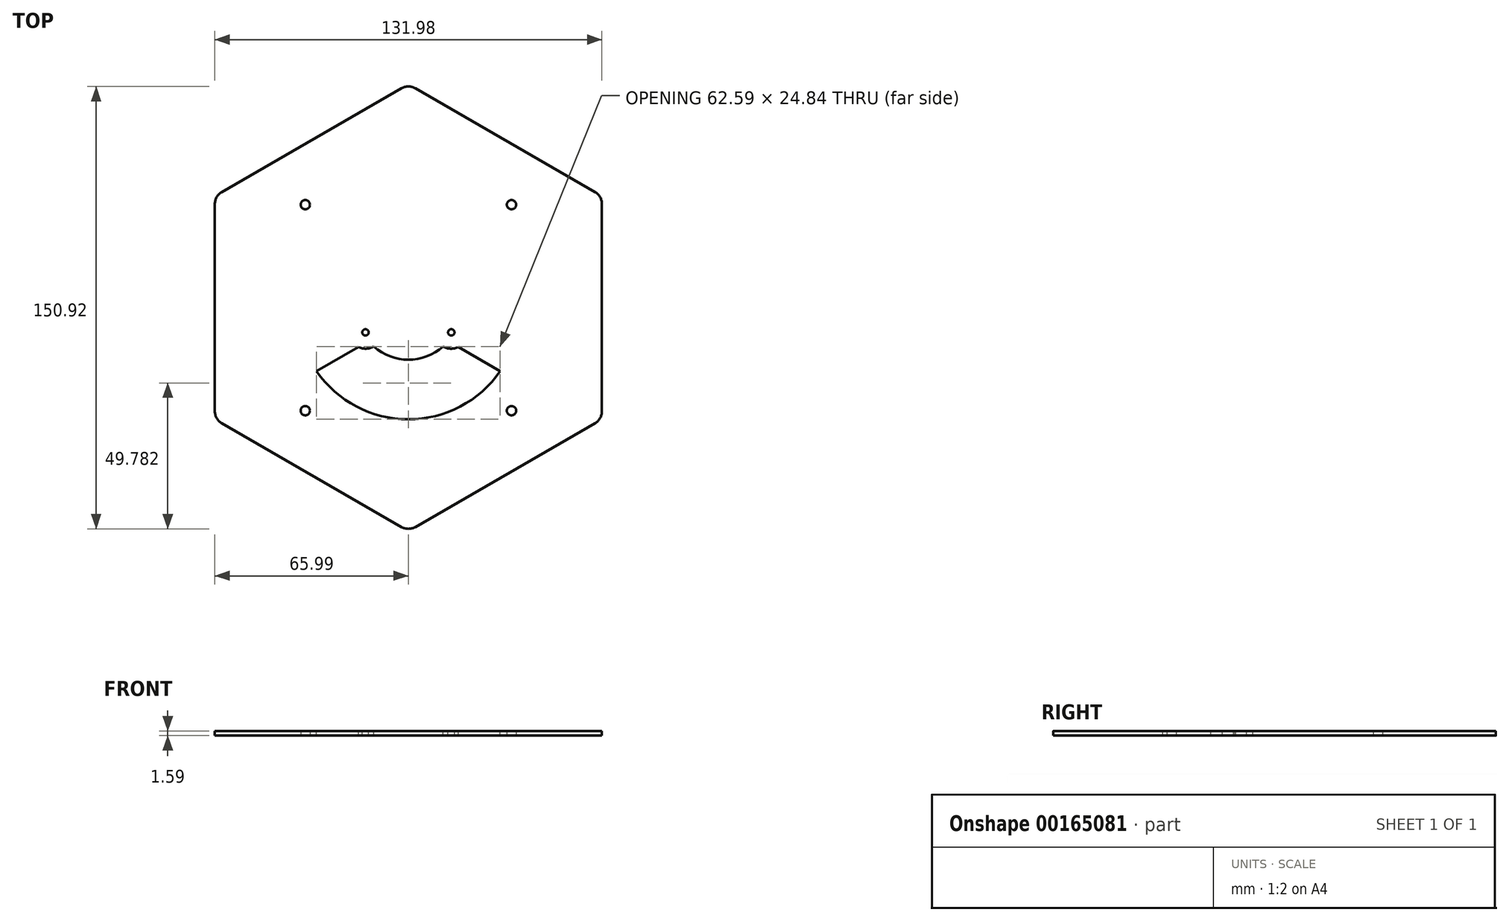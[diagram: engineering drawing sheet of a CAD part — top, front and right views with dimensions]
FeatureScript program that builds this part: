
annotation { "Feature Type Name" : "Feature", "Feature Type Description" : "" }
export const myFeature = defineFeature(function(context is Context, id is Id, definition is map)
    precondition{}
    {
        {
            var Q0;
            Q0=qCreatedBy(makeId("Top.planeOp"),FACE);
            var sketch = newSketch(context, id + "F0", { "sketchPlane" : qUnion([Q0])});
            skLineSegment(sketch, "E0.bottom", {"start": v(35.15, -35.15) * mm, "end": v(35.15, 35.15) * mm, "construction": true});
            skLineSegment(sketch, "E0.top", {"start": v(-35.15, -35.15) * mm, "end": v(-35.15, 35.15) * mm, "construction": true});
            skLineSegment(sketch, "E0.left", {"start": v(35.15, -35.15) * mm, "end": v(-35.15, -35.15) * mm, "construction": true});
            skLineSegment(sketch, "E0.right", {"start": v(35.15, 35.15) * mm, "end": v(-35.15, 35.15) * mm, "construction": true});
            skPoint(sketch, "E0.middle", {"position": v(0, 0) * mm});
            skCircle(sketch, "E1", {"center": v(0, 0) * mm, "radius": 38.1 * mm, "construction": true});
            skCircle(sketch, "E2", {"center": v(35.15, -35.15) * mm, "radius": 1.59 * mm});
            skCircle(sketch, "E3", {"center": v(35.15, 35.15) * mm, "radius": 1.59 * mm});
            skCircle(sketch, "E4", {"center": v(-35.15, 35.15) * mm, "radius": 1.59 * mm});
            skCircle(sketch, "E5", {"center": v(-35.15, -35.15) * mm, "radius": 1.59 * mm});
            skCircle(sketch, "E6", {"center": v(35.15, -35.15) * mm, "radius": 4.53 * mm, "construction": true});
            skCircle(sketch, "E7.cCircle", {"center": v(0, 0) * mm, "radius": 66 * mm, "construction": true});
            skLineSegment(sketch, "E7.0", {"start": v(66, 38.1) * mm, "end": v(66, -38.1) * mm});
            skLineSegment(sketch, "E7.1", {"start": v(66, -38.1) * mm, "end": v(0, -76.2) * mm});
            skLineSegment(sketch, "E7.2", {"start": v(0, -76.2) * mm, "end": v(-66, -38.1) * mm});
            skLineSegment(sketch, "E7.3", {"start": v(-66, -38.1) * mm, "end": v(-66, 38.1) * mm});
            skLineSegment(sketch, "E7.4", {"start": v(-66, 38.1) * mm, "end": v(0, 76.2) * mm});
            skLineSegment(sketch, "E7.5", {"start": v(0, 76.2) * mm, "end": v(66, 38.1) * mm});
            skPoint(sketch, "E7.0.midPoint", {"position": v(66, 0) * mm});
            skCircle(sketch, "E8.cCircle", {"center": v(0, 0) * mm, "radius": 52.55 * mm, "construction": true});
            skLineSegment(sketch, "E8.0", {"start": v(52.55, 30.34) * mm, "end": v(52.55, -30.34) * mm, "construction": true});
            skLineSegment(sketch, "E8.1", {"start": v(52.55, -30.34) * mm, "end": v(0, -60.68) * mm, "construction": true});
            skLineSegment(sketch, "E8.2", {"start": v(0, -60.68) * mm, "end": v(-52.55, -30.34) * mm, "construction": true});
            skLineSegment(sketch, "E8.3", {"start": v(-52.55, -30.34) * mm, "end": v(-52.55, 30.34) * mm, "construction": true});
            skLineSegment(sketch, "E8.4", {"start": v(-52.55, 30.34) * mm, "end": v(0, 60.68) * mm, "construction": true});
            skLineSegment(sketch, "E8.5", {"start": v(0, 60.68) * mm, "end": v(52.55, 30.34) * mm, "construction": true});
            skPoint(sketch, "E8.0.midPoint", {"position": v(52.55, 0) * mm});
            skSolve(sketch);
        }
        {
            var Q0;
            Q0=makeQuery(id+"F0.imprint","IMPRINT",FACE,{"disambiguationData":[TD([[makeQuery(id+"F0.imprint","IMPRINT",EDGE,{"derivedFrom":sQuery(id+"F0.wireOp",EDGE,"E1")}),-1.0]])]});
            var Q1;
            Q1=makeQuery(id+"F0.imprint","IMPRINT",FACE,{"disambiguationData":[TD([[makeQuery(id+"F0.imprint","IMPRINT",EDGE,{"derivedFrom":sQuery(id+"F0.wireOp",EDGE,"E2")}),-1.0]])]});
            extrude(context, id + "F1", {"entities" : qUnion([Q0, Q1]), "depth" : 1.59 * mm});
        }
        {
            var Q0;
            Q0=makeQuery(id+"F1.opExtrude","CAP_FACE",FACE,{"disambiguationData":[OSD([sQuery(id+"F0.wireOp",EDGE,"E2"),sQuery(id+"F0.wireOp",EDGE,"E3"),sQuery(id+"F0.wireOp",EDGE,"E4"),sQuery(id+"F0.wireOp",EDGE,"E5"),sQuery(id+"F0.wireOp",EDGE,"R1JFTZ4v-WKVF-8XfW-xGAy-tLIKOYTsBxTY.bottom"),sQuery(id+"F0.wireOp",EDGE,"R1JFTZ4v-WKVF-8XfW-xGAy-tLIKOYTsBxTY.top"),sQuery(id+"F0.wireOp",EDGE,"R1JFTZ4v-WKVF-8XfW-xGAy-tLIKOYTsBxTY.left"),sQuery(id+"F0.wireOp",EDGE,"R1JFTZ4v-WKVF-8XfW-xGAy-tLIKOYTsBxTY.right")])],"isStart":false});
            var sketch = newSketch(context, id + "F2", { "sketchPlane" : qUnion([Q0])});
            skArc(sketch, "E9", {"start": v(-11.85, -13.26) * mm, "mid": v(0, -17.78) * mm, "end": v(11.85, -13.26) * mm});
            skArc(sketch, "E10", {"start": v(-31.3, -21.73) * mm, "mid": v(0, -38.1) * mm, "end": v(31.3, -21.73) * mm});
            skLineSegment(sketch, "E11", {"start": v(0, -17.78) * mm, "end": v(0, 0) * mm, "construction": true});
            skArc(sketch, "E12", {"start": v(11.85, -13.26) * mm, "mid": v(14.4, -14) * mm, "end": v(16.99, -13.47) * mm});
            skLineSegment(sketch, "E13", {"start": v(11.85, -13.26) * mm, "end": v(14.63, -8.44) * mm, "construction": true});
            skCircle(sketch, "E14", {"center": v(14.63, -8.44) * mm, "radius": 1.1 * mm});
            skLineSegment(sketch, "E15", {"start": v(16.99, -13.47) * mm, "end": v(31.3, -21.73) * mm});
            skLineSegment(sketch, "E16", {"start": v(0, 0) * mm, "end": v(14.63, -8.44) * mm, "construction": true});
            skLineSegment(sketch, "E17", {"start": v(14.63, -8.44) * mm, "end": v(25.73, -14.85) * mm, "construction": true});
            skLineSegment(sketch, "E18", {"start": v(25.73, -14.85) * mm, "end": v(24.14, -17.6) * mm, "construction": true});
            skLineSegment(sketch, "E19", {"start": v(-11.85, -13.26) * mm, "end": v(-14.63, -8.44) * mm, "construction": true});
            skLineSegment(sketch, "E20", {"start": v(-31.3, -21.73) * mm, "end": v(-16.99, -13.47) * mm});
            skArc(sketch, "E21", {"start": v(-16.99, -13.47) * mm, "mid": v(-14.4, -14) * mm, "end": v(-11.85, -13.26) * mm});
            skCircle(sketch, "E22", {"center": v(-14.63, -8.44) * mm, "radius": 1.1 * mm});
            skLineSegment(sketch, "E23", {"start": v(0, 0) * mm, "end": v(-14.63, -8.44) * mm, "construction": true});
            skLineSegment(sketch, "E24", {"start": v(-14.63, -8.44) * mm, "end": v(-25.73, -14.85) * mm, "construction": true});
            skLineSegment(sketch, "E25", {"start": v(-25.73, -14.85) * mm, "end": v(-24.14, -17.6) * mm, "construction": true});
            skSolve(sketch);
        }
        {
            var Q0;
            Q0=qSketchRegion(id+"F2",true);
            var Q1;
            Q1=makeQuery(id+"F1.opExtrude","CAP_FACE",FACE,{"disambiguationData":[OSD([sQuery(id+"F0.wireOp",EDGE,"E2"),sQuery(id+"F0.wireOp",EDGE,"E3"),sQuery(id+"F0.wireOp",EDGE,"E4"),sQuery(id+"F0.wireOp",EDGE,"E5"),sQuery(id+"F0.wireOp",EDGE,"R1JFTZ4v-WKVF-8XfW-xGAy-tLIKOYTsBxTY.bottom"),sQuery(id+"F0.wireOp",EDGE,"R1JFTZ4v-WKVF-8XfW-xGAy-tLIKOYTsBxTY.top"),sQuery(id+"F0.wireOp",EDGE,"R1JFTZ4v-WKVF-8XfW-xGAy-tLIKOYTsBxTY.left"),sQuery(id+"F0.wireOp",EDGE,"R1JFTZ4v-WKVF-8XfW-xGAy-tLIKOYTsBxTY.right")])],"isStart":true});
            extrude(context, id + "F3", {"entities" : qUnion([Q0]), "operationType" : NewBodyOperationType.REMOVE, "endBound" : BoundingType.UP_TO_SURFACE, "oppositeDirection" : true, "endBoundEntityFace" : qUnion([Q1]), "depth" : 25.4 * mm});
        }
        {
            var Q0;
            Q0=makeQuery(id+"F1.opExtrude","SWEPT_EDGE",EDGE,{"disambiguationData":[OSD([sQuery(id+"F0.wireOp",EDGE,"E7.3"),sQuery(id+"F0.wireOp",EDGE,"E7.4")])]});
            var Q1;
            Q1=makeQuery(id+"F1.opExtrude","SWEPT_EDGE",EDGE,{"disambiguationData":[OSD([sQuery(id+"F0.wireOp",EDGE,"E7.4"),sQuery(id+"F0.wireOp",EDGE,"E7.5")])]});
            var Q2;
            Q2=makeQuery(id+"F1.opExtrude","SWEPT_EDGE",EDGE,{"disambiguationData":[OSD([sQuery(id+"F0.wireOp",EDGE,"E7.0"),sQuery(id+"F0.wireOp",EDGE,"E7.5")])]});
            var Q3;
            Q3=makeQuery(id+"F1.opExtrude","SWEPT_EDGE",EDGE,{"disambiguationData":[OSD([sQuery(id+"F0.wireOp",EDGE,"E7.0"),sQuery(id+"F0.wireOp",EDGE,"E7.1")])]});
            var Q4;
            Q4=makeQuery(id+"F1.opExtrude","SWEPT_EDGE",EDGE,{"disambiguationData":[OSD([sQuery(id+"F0.wireOp",EDGE,"E7.1"),sQuery(id+"F0.wireOp",EDGE,"E7.2")])]});
            var Q5;
            Q5=makeQuery(id+"F1.opExtrude","SWEPT_EDGE",EDGE,{"disambiguationData":[OSD([sQuery(id+"F0.wireOp",EDGE,"E7.2"),sQuery(id+"F0.wireOp",EDGE,"E7.3")])]});
            fillet(context, id + "F4", {"entities" : qUnion([Q0, Q1, Q2, Q3, Q4, Q5]), "radius" : 4.76 * mm, "tangentPropagation" : true, "allowEdgeOverflow" : false});
        }
    });
